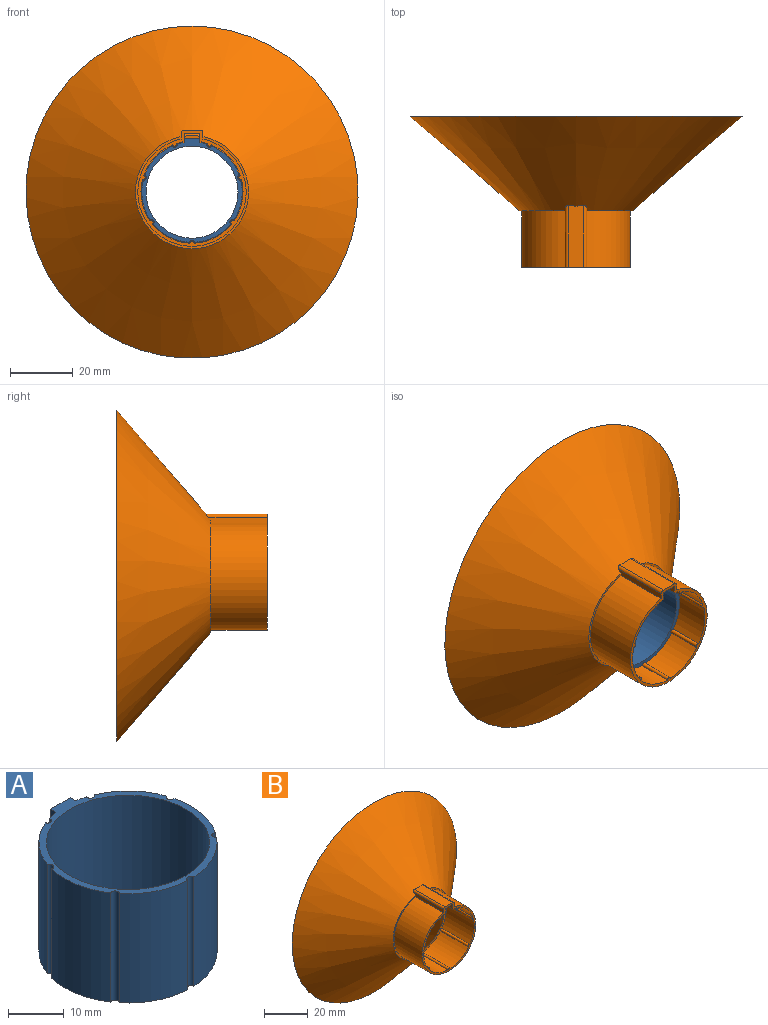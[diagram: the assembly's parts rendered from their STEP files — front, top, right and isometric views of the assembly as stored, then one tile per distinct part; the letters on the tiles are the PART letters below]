
ASSEMBLY  parts=2 mates=1
PART A: 22 faces, bbox 32x33.1x24 mm
  f0: cylinder r=14.65mm len=29.3mm, axis (0,0,1), area 2206.6mm2, adj f19,f20,f21
  f1: plane 24x1.35mm, normal (-1,0,0), area 32.3mm2, adj f2,f18,f19,f20
  f2: cylinder r=16mm len=24mm, axis (0,0,1), area 55.8mm2, adj f1,f3,f19,f20
  f3: cylinder r=0.75mm len=24mm, axis (0,0,1), area 55.7mm2, adj f2,f4,f19,f20
  f4: cylinder r=16mm len=24mm, axis (0,0,1), area 321.4mm2, adj f3,f5,f19,f20
  f5: cylinder r=0.75mm len=24mm, axis (0,0,1), area 55.7mm2, adj f4,f6,f19,f20
  f6: cylinder r=16mm len=24mm, axis (0,0,1), area 321.4mm2, adj f5,f7,f19,f20
  f7: cylinder r=0.75mm len=24mm, axis (0,0,1), area 55.7mm2, adj f6,f8,f19,f20
  f8: cylinder r=16mm len=24mm, axis (0,0,1), area 321.4mm2, adj f7,f9,f19,f20
  f9: cylinder r=0.75mm len=24mm, axis (0,0,1), area 55.7mm2, adj f8,f10,f19,f20
  f10: cylinder r=16mm len=24mm, axis (0,0,1), area 321.4mm2, adj f9,f11,f19,f20
  f11: cylinder r=0.75mm len=24mm, axis (0,0,1), area 55.7mm2, adj f10,f12,f19,f20
  f12: cylinder r=16mm len=24mm, axis (0,0,1), area 321.4mm2, adj f11,f13,f19,f20
  f13: cylinder r=0.75mm len=24mm, axis (0,0,1), area 55.7mm2, adj f12,f14,f19,f20
  f14: cylinder r=16mm len=24mm, axis (0,0,1), area 321.4mm2, adj f13,f15,f19,f20
  f15: cylinder r=0.75mm len=24mm, axis (0,0,1), area 55.7mm2, adj f14,f16,f19,f20
  f16: cylinder r=16mm len=24mm, axis (0,0,1), area 55.8mm2, adj f15,f17,f19,f20
  f17: plane 24x1.35mm, normal (1,0,0), area 32.3mm2, adj f16,f18,f19,f20
  f18: plane 24x5mm, normal (0,1,0), area 117.5mm2, adj f1,f17,f19,f20,f21
  f19: plane 33.13x32mm, normal (0,0,-1), area 129.9mm2, adj f0,f1,f2,f3,f4,f5,f6,f7
  f20: plane 33.13x32mm, normal (0,0,1), area 129.9mm2, adj f0,f1,f2,f3,f4,f5,f6,f7
  f21: cylinder r=0.9mm len=2.53mm, axis (0,1,0), area 14.2mm2, adj f0,f18
PART B: 31 faces, bbox 106.2x48.4x106.2 mm
  f0: plane 36x35.66mm, normal (0,-1,0), area 77.8mm2, adj f1,f20,f21,f22
  f1: cone r=18mm half-angle=49.3deg, axis (0,1,0), area 10225mm2, adj f0,f2,f20,f22,f23,f25,f26
  f2: plane 105.74x105.74mm, normal (0,1,0), area 438.7mm2, adj f1,f30
  f3: cylinder r=16.25mm len=18mm, axis (0,-1,0), area 44.8mm2, adj f4,f24,f27,f29
  f4: cylinder r=0.68mm len=18mm, axis (0,-1,0), area 37.7mm2, adj f3,f5,f27,f29
  f5: cylinder r=16.25mm len=18mm, axis (0,-1,0), area 248mm2, adj f4,f6,f27,f29
  f6: cylinder r=0.68mm len=18mm, axis (0,-1,0), area 37.7mm2, adj f5,f7,f27,f29
  f7: cylinder r=16.25mm len=18mm, axis (0,-1,0), area 248mm2, adj f6,f8,f27,f29
  f8: cylinder r=0.68mm len=18mm, axis (0,-1,0), area 37.7mm2, adj f7,f9,f27,f29
  f9: cylinder r=16.25mm len=18mm, axis (0,-1,0), area 248mm2, adj f8,f10,f27,f29
  f10: cylinder r=0.68mm len=18mm, axis (0,-1,0), area 37.7mm2, adj f9,f11,f27,f29
  f11: cylinder r=16.25mm len=18mm, axis (0,-1,0), area 248mm2, adj f10,f12,f27,f29
  f12: cylinder r=0.68mm len=18mm, axis (0,-1,0), area 37.7mm2, adj f11,f13,f27,f29
  f13: cylinder r=16.25mm len=18mm, axis (0,-1,0), area 248mm2, adj f12,f14,f27,f29
  f14: cylinder r=0.68mm len=18mm, axis (0,-1,0), area 37.7mm2, adj f13,f15,f27,f29
  f15: cylinder r=16.25mm len=18mm, axis (0,-1,0), area 248mm2, adj f14,f16,f27,f29
  f16: cylinder r=0.68mm len=18mm, axis (0,-1,0), area 37.7mm2, adj f15,f17,f27,f29
  f17: cylinder r=16.25mm len=18mm, axis (0,-1,0), area 44.8mm2, adj f16,f18,f27,f29
  f18: plane 18.79x2.7mm, normal (1,0,0), area 48.8mm2, adj f17,f19,f27,f28,f29
  f19: plane 19.23x5.45mm, normal (0,0,-1), area 93.5mm2, adj f18,f24,f27,f28
  f20: plane 18.93x1.86mm, normal (-1,0,0), area 34mm2, adj f0,f1,f21,f26,f27
  f21: cylinder r=17.25mm len=34.5mm, axis (0,-1,0), area 1824mm2, adj f0,f20,f22,f27
  f22: plane 18.93x1.86mm, normal (1,0,0), area 34mm2, adj f0,f1,f21,f25,f27
  f23: plane 19.75x5.11mm, normal (0,0,1), area 97.8mm2, adj f1,f25,f26,f27
  f24: plane 18.79x2.7mm, normal (-1,0,0), area 48.8mm2, adj f3,f19,f27,f28,f29
  f25: cylinder r=1mm len=19.64mm, axis (0,-1,0), area 30.3mm2, adj f1,f22,f23,f27
  f26: cylinder r=1mm len=19.64mm, axis (0,-1,0), area 30.3mm2, adj f1,f20,f23,f27
  f27: plane 37x34.5mm, normal (0,-1,0), area 115.3mm2, adj f3,f4,f5,f6,f7,f8,f9,f10
  f28: cone r=18mm half-angle=49.3deg, axis (0,1,0), area 6.1mm2, adj f18,f19,f24,f29
  f29: plane 34.24x32.5mm, normal (0,-1,0), area 126.5mm2, adj f3,f4,f5,f6,f7,f8,f9,f10
  f30: cone r=15mm half-angle=50.6deg, axis (0,1,0), area 9881mm2, adj f2,f29
PLACE A rot(axis=(1,0,0),90deg) t=(24.25,-2.22,40.09)mm fixed
PLACE B rot(axis=(0,-1,0),0deg) t=(24.25,-13.43,40.09)mm
MATE slider A.f0 <-> B.f1  axis (0,-1,0) through (-5.75,-2.22,10.09)mm
